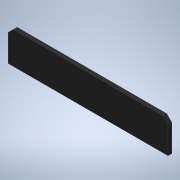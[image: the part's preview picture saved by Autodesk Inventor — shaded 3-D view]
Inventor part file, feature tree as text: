
AUTODESK INVENTOR PART (.ipt)
format: ipt  version: 2020 (Build 240168000, 168)  size: 111,616 bytes
history: native  units: mm
features: other x1, extrude x1, chamfer x1
ambient origin geometry x8: Origin, YZ Plane, XZ Plane, XY Plane, X Axis, Y Axis, Z Axis, Center Point
bodies: Body1 (feature_tree)
feature tree (3):
  other  "實體1"
  extrude  "擠出1"  Depth=25.0mm
  chamfer  "倒角1"  Distance=125.0mm
